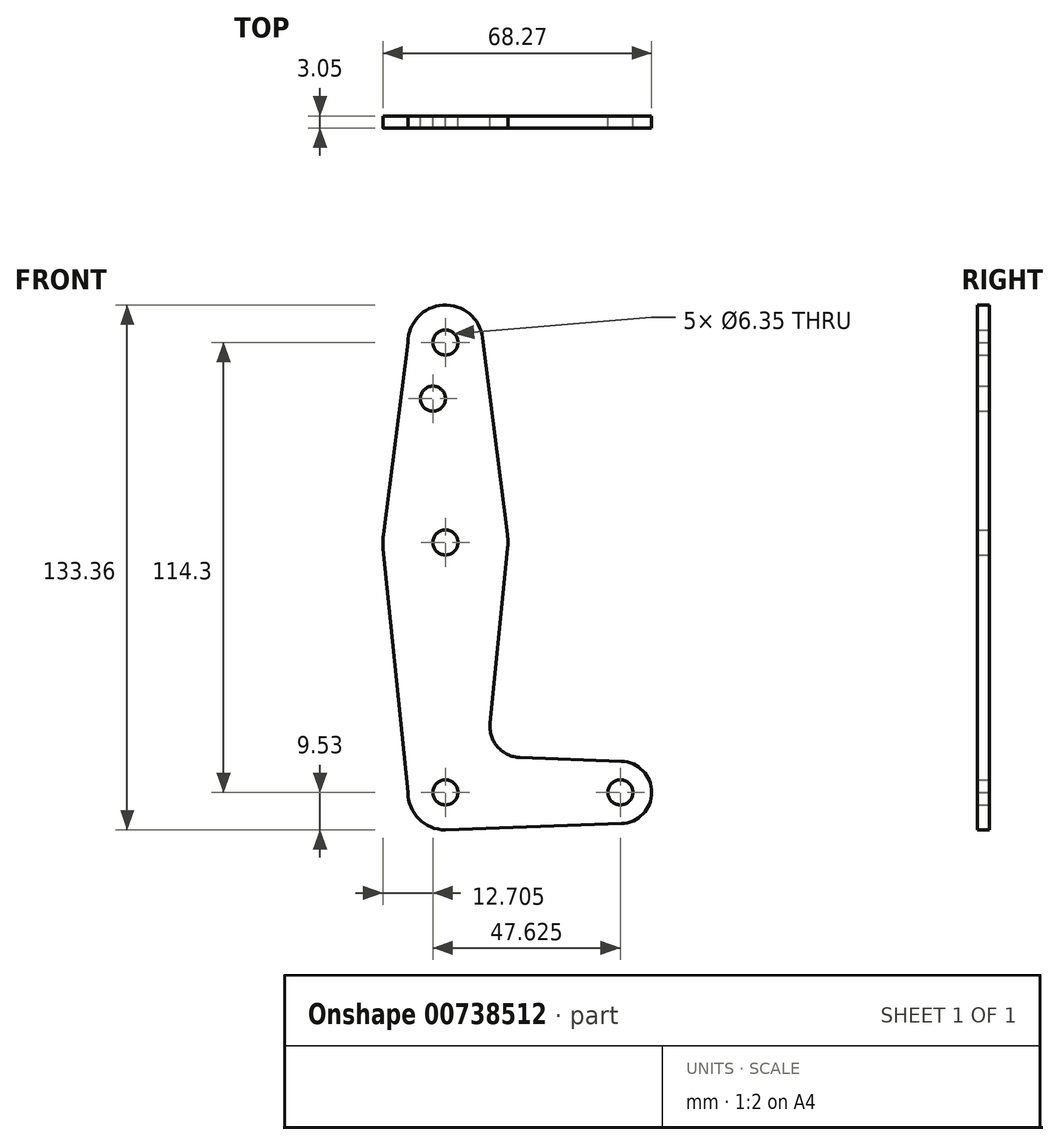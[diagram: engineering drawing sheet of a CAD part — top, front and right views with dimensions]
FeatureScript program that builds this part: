
annotation { "Feature Type Name" : "Feature", "Feature Type Description" : "" }
export const myFeature = defineFeature(function(context is Context, id is Id, definition is map)
    precondition{}
    {
        {
            var Q0;
            Q0=qCreatedBy(makeId("Front.planeOp"),FACE);
            var sketch = newSketch(context, id + "F0", { "sketchPlane" : qUnion([Q0])});
            skLineSegment(sketch, "E0", {"start": v(0, 0) * mm, "end": v(0, 63.5) * mm, "construction": true});
            skLineSegment(sketch, "E1", {"start": v(0, 63.5) * mm, "end": v(0, 114.3) * mm, "construction": true});
            skLineSegment(sketch, "E2", {"start": v(0, 0) * mm, "end": v(44.45, 0) * mm, "construction": true});
            skCircle(sketch, "E3", {"center": v(0, 114.3) * mm, "radius": 9.53 * mm});
            skCircle(sketch, "E4", {"center": v(0, 63.5) * mm, "radius": 15.88 * mm});
            skCircle(sketch, "E5", {"center": v(0, 0) * mm, "radius": 9.53 * mm});
            skCircle(sketch, "E6", {"center": v(44.45, 0) * mm, "radius": 7.94 * mm});
            skLineSegment(sketch, "E7", {"start": v(-9.52, 114.3) * mm, "end": v(-15.75, 65.5) * mm});
            skLineSegment(sketch, "E8", {"start": v(9.45, 115.5) * mm, "end": v(15.75, 65.48) * mm});
            skLineSegment(sketch, "E9", {"start": v(15.8, 61.91) * mm, "end": v(11.34, 17.6) * mm});
            skLineSegment(sketch, "E10", {"start": v(18.97, 8.85) * mm, "end": v(44.73, 7.93) * mm});
            skLineSegment(sketch, "E11", {"start": v(0, -9.53) * mm, "end": v(44.73, -7.93) * mm});
            skLineSegment(sketch, "E12", {"start": v(-9.53, 0) * mm, "end": v(-15.8, 61.9) * mm});
            skCircle(sketch, "E13", {"center": v(0, 114.3) * mm, "radius": 3.18 * mm});
            skCircle(sketch, "E14", {"center": v(-3.18, 100.03) * mm, "radius": 3.18 * mm});
            skCircle(sketch, "E15", {"center": v(0, 63.5) * mm, "radius": 3.18 * mm});
            skCircle(sketch, "E16", {"center": v(0, 0) * mm, "radius": 3.18 * mm});
            skCircle(sketch, "E17", {"center": v(44.45, 0) * mm, "radius": 3.18 * mm});
            skArc(sketch, "E18.filletArc", {"start": v(11.34, 17.6) * mm, "mid": v(13.26, 11.57) * mm, "end": v(18.97, 8.85) * mm});
            skSolve(sketch);
        }
        {
            var Q0;
            Q0=makeQuery(id+"F0.imprint","IMPRINT",FACE,{"disambiguationData":[TD([[makeQuery(id+"F0.imprint","IMPRINT",EDGE,{"derivedFrom":sQuery(id+"F0.wireOp",EDGE,"E13")}),-1.0]])]});
            var Q1;
            {var subQ1=sQuery(id+"F0.wireOp",EDGE,"E7");Q1=makeQuery(id+"F0.imprint","IMPRINT",FACE,{"disambiguationData":[TD([[makeQuery(id+"F0.imprint","IMPRINT",EDGE,{"derivedFrom":subQ1}),1.0]])]});}
            var Q2;
            Q2=makeQuery(id+"F0.imprint","IMPRINT",FACE,{"disambiguationData":[TD([[makeQuery(id+"F0.imprint","IMPRINT",EDGE,{"derivedFrom":sQuery(id+"F0.wireOp",EDGE,"E15")}),-1.0]])]});
            var Q3;
            {var subQ0=sQuery(id+"F0.wireOp",EDGE,"E9");Q3=makeQuery(id+"F0.imprint","IMPRINT",FACE,{"disambiguationData":[TD([[makeQuery(id+"F0.imprint","IMPRINT",EDGE,{"derivedFrom":subQ0}),-1.0]])]});}
            var Q4;
            Q4=makeQuery(id+"F0.imprint","IMPRINT",FACE,{"disambiguationData":[TD([[makeQuery(id+"F0.imprint","IMPRINT",EDGE,{"derivedFrom":sQuery(id+"F0.wireOp",EDGE,"E16")}),-1.0]])]});
            var Q5;
            Q5=makeQuery(id+"F0.imprint","IMPRINT",FACE,{"disambiguationData":[TD([[makeQuery(id+"F0.imprint","IMPRINT",EDGE,{"derivedFrom":sQuery(id+"F0.wireOp",EDGE,"E17")}),-1.0]])]});
            extrude(context, id + "F1", {"entities" : qUnion([Q0, Q1, Q2, Q3, Q4, Q5]), "depth" : 3.05 * mm, "offsetDistance" : 25.4 * mm});
        }
    });
